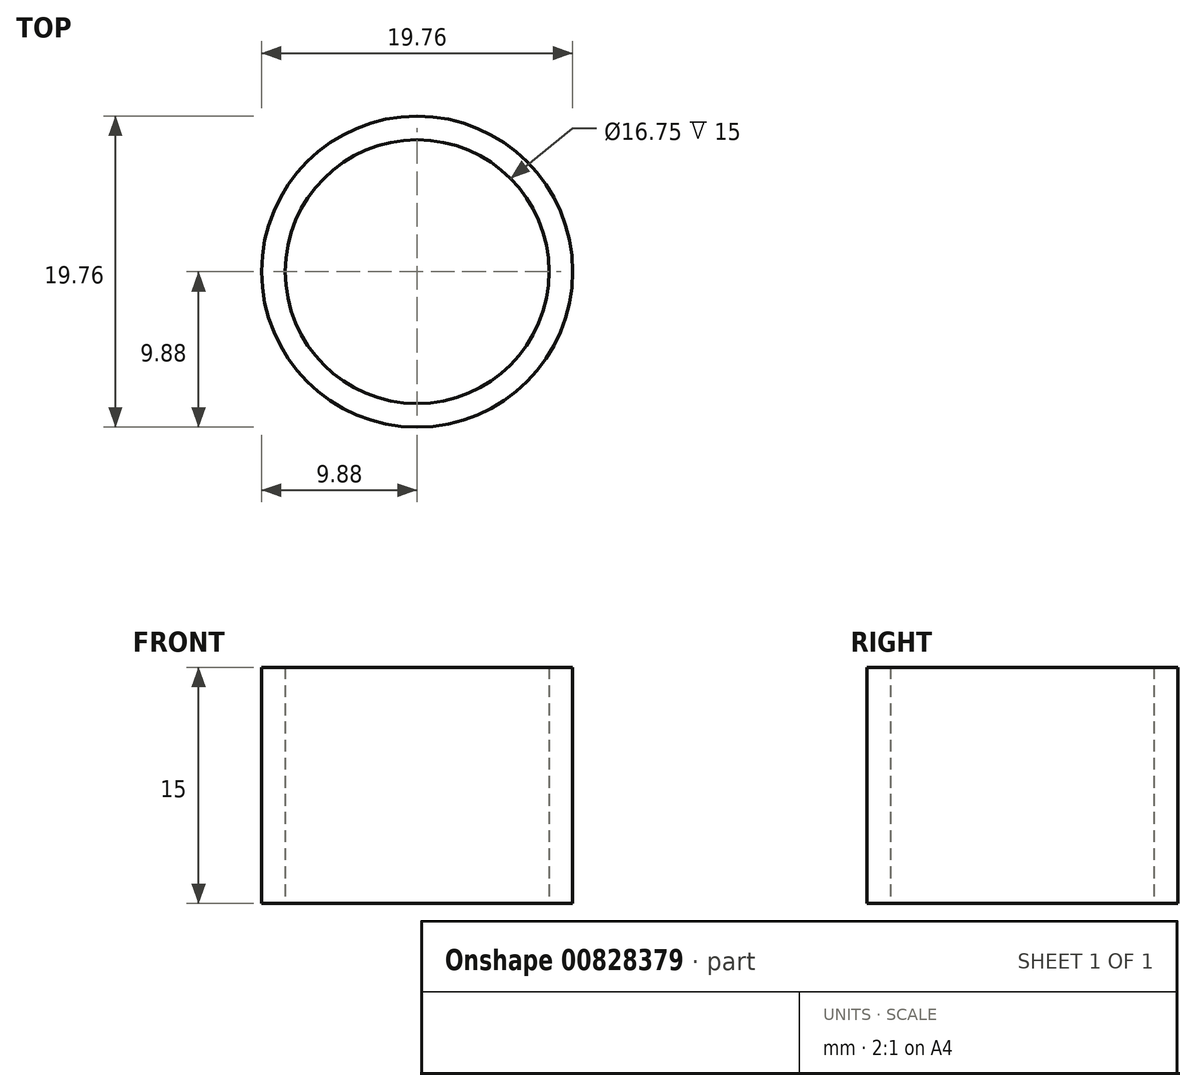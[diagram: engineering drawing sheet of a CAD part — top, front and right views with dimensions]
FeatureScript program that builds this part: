
annotation { "Feature Type Name" : "Feature", "Feature Type Description" : "" }
export const myFeature = defineFeature(function(context is Context, id is Id, definition is map)
    precondition{}
    {
        {
            var Q0;
            Q0=qCreatedBy(makeId("Top.planeOp"),FACE);
            var sketch = newSketch(context, id + "F0", { "sketchPlane" : qUnion([Q0])});
            skCircle(sketch, "E0", {"center": v(0, 0) * mm, "radius": 8.38 * mm});
            skCircle(sketch, "E1.0", {"center": v(0, 0) * mm, "radius": 9.88 * mm});
            skSolve(sketch);
        }
        {
            var Q0;
            Q0=makeQuery(id+"F0.imprint","IMPRINT",FACE,{"disambiguationData":[TD([[makeQuery(id+"F0.imprint","IMPRINT",EDGE,{"derivedFrom":sQuery(id+"F0.wireOp",EDGE,"E0")}),-1.0]])]});
            extrude(context, id + "F1", {"entities" : qUnion([Q0]), "depth" : 15 * mm, "offsetDistance" : 25 * mm});
        }
    });
